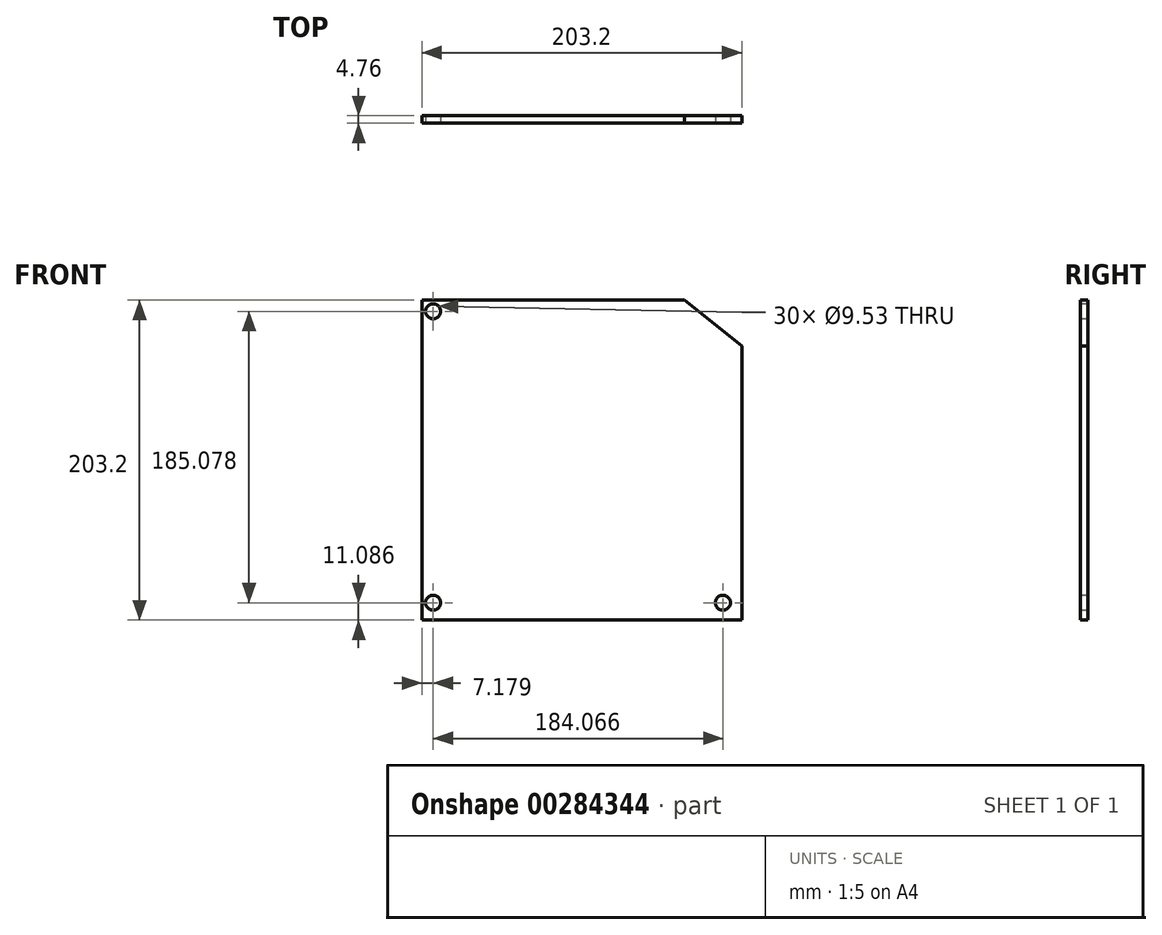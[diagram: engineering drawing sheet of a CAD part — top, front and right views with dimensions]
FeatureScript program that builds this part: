
annotation { "Feature Type Name" : "Feature", "Feature Type Description" : "" }
export const myFeature = defineFeature(function(context is Context, id is Id, definition is map)
    precondition{}
    {
        {
            var Q0;
            Q0=qCreatedBy(makeId("Front.planeOp"),FACE);
            var sketch = newSketch(context, id + "F0", { "sketchPlane" : qUnion([Q0])});
            skLineSegment(sketch, "E0.bottom", {"start": v(-171.49, 95.16) * mm, "end": v(31.71, 95.16) * mm});
            skLineSegment(sketch, "E0.top", {"start": v(-171.49, -108.04) * mm, "end": v(31.71, -108.04) * mm});
            skLineSegment(sketch, "E0.left", {"start": v(-171.49, 95.16) * mm, "end": v(-171.49, -108.04) * mm});
            skLineSegment(sketch, "E0.right", {"start": v(31.71, 95.16) * mm, "end": v(31.71, -108.04) * mm});
            skSolve(sketch);
        }
        {
            var Q0;
            Q0=makeQuery(id+"F0.imprint","IMPRINT",FACE,{"disambiguationData":[TD([[makeQuery(id+"F0.imprint","IMPRINT",EDGE,{"derivedFrom":sQuery(id+"F0.wireOp",EDGE,"E0.bottom")}),-1.0]])]});
            extrude(context, id + "F1", {"entities" : qUnion([Q0]), "depth" : 4.76 * mm});
        }
        {
            var Q0;
            Q0=makeQuery(id+"F1.opExtrude","CAP_FACE",FACE,{"disambiguationData":[OSD([sQuery(id+"F0.wireOp",EDGE,"E0.bottom"),sQuery(id+"F0.wireOp",EDGE,"E0.top"),sQuery(id+"F0.wireOp",EDGE,"E0.left"),sQuery(id+"F0.wireOp",EDGE,"E0.right")])],"isStart":false});
            var sketch = newSketch(context, id + "F2", { "sketchPlane" : qUnion([Q0])});
            skLineSegment(sketch, "E1", {"start": v(-4.52, 95.16) * mm, "end": v(31.71, 66.21) * mm});
            skSolve(sketch);
        }
        {
            var Q0;
            {var subQ0=sQuery(id+"F2.wireOp",EDGE,"E1");Q0=makeQuery(id+"F2.imprint","IMPRINT",FACE,{"disambiguationData":[TD([[makeQuery(id+"F2.imprint","IMPRINT",EDGE,{"derivedFrom":subQ0}),1.0]])]});}
            extrude(context, id + "F3", {"entities" : qUnion([Q0]), "operationType" : NewBodyOperationType.REMOVE, "oppositeDirection" : true, "depth" : 25.4 * mm});
        }
        {
            var Q0;
            Q0=makeQuery(id+"F1.opExtrude","CAP_FACE",FACE,{"disambiguationData":[OSD([sQuery(id+"F0.wireOp",EDGE,"E0.bottom"),sQuery(id+"F0.wireOp",EDGE,"E0.top"),sQuery(id+"F0.wireOp",EDGE,"E0.left"),sQuery(id+"F0.wireOp",EDGE,"E0.right")])],"isStart":false});
            var sketch = newSketch(context, id + "F4", { "sketchPlane" : qUnion([Q0])});
            skPoint(sketch, "E2", {"position": v(-164.31, 88.12) * mm});
            skPoint(sketch, "E3", {"position": v(-164.31, -96.95) * mm});
            skPoint(sketch, "E4", {"position": v(19.75, -96.95) * mm});
            skSolve(sketch);
        }
        {
            var Q0;
            Q0=sQuery(id+"F4.wireOp",VERTEX,"E2");
            var Q1;
            Q1=sQuery(id+"F4.wireOp",VERTEX,"E3");
            var Q2;
            Q2=sQuery(id+"F4.wireOp",VERTEX,"E4");
            var Q3;
            Q3=makeQuery(id+"F1.opExtrude","SWEPT_BODY",BODY,{"disambiguationData":[OSD([sQuery(id+"F0.wireOp",EDGE,"E0.bottom"),sQuery(id+"F0.wireOp",EDGE,"E0.top"),sQuery(id+"F0.wireOp",EDGE,"E0.left"),sQuery(id+"F0.wireOp",EDGE,"E0.right")])]});
            hole(context, id + "F5", {"style" : HoleStyle.SIMPLE, "endStyle" : HoleEndStyle.THROUGH, "holeDiameter" : 9.52 * mm, "tappedDepth" : 12.7 * mm, "tapClearance" : 3, "locations" : qUnion([Q0, Q1, Q2]), "scope" : qUnion([Q3])});
        }
    });
